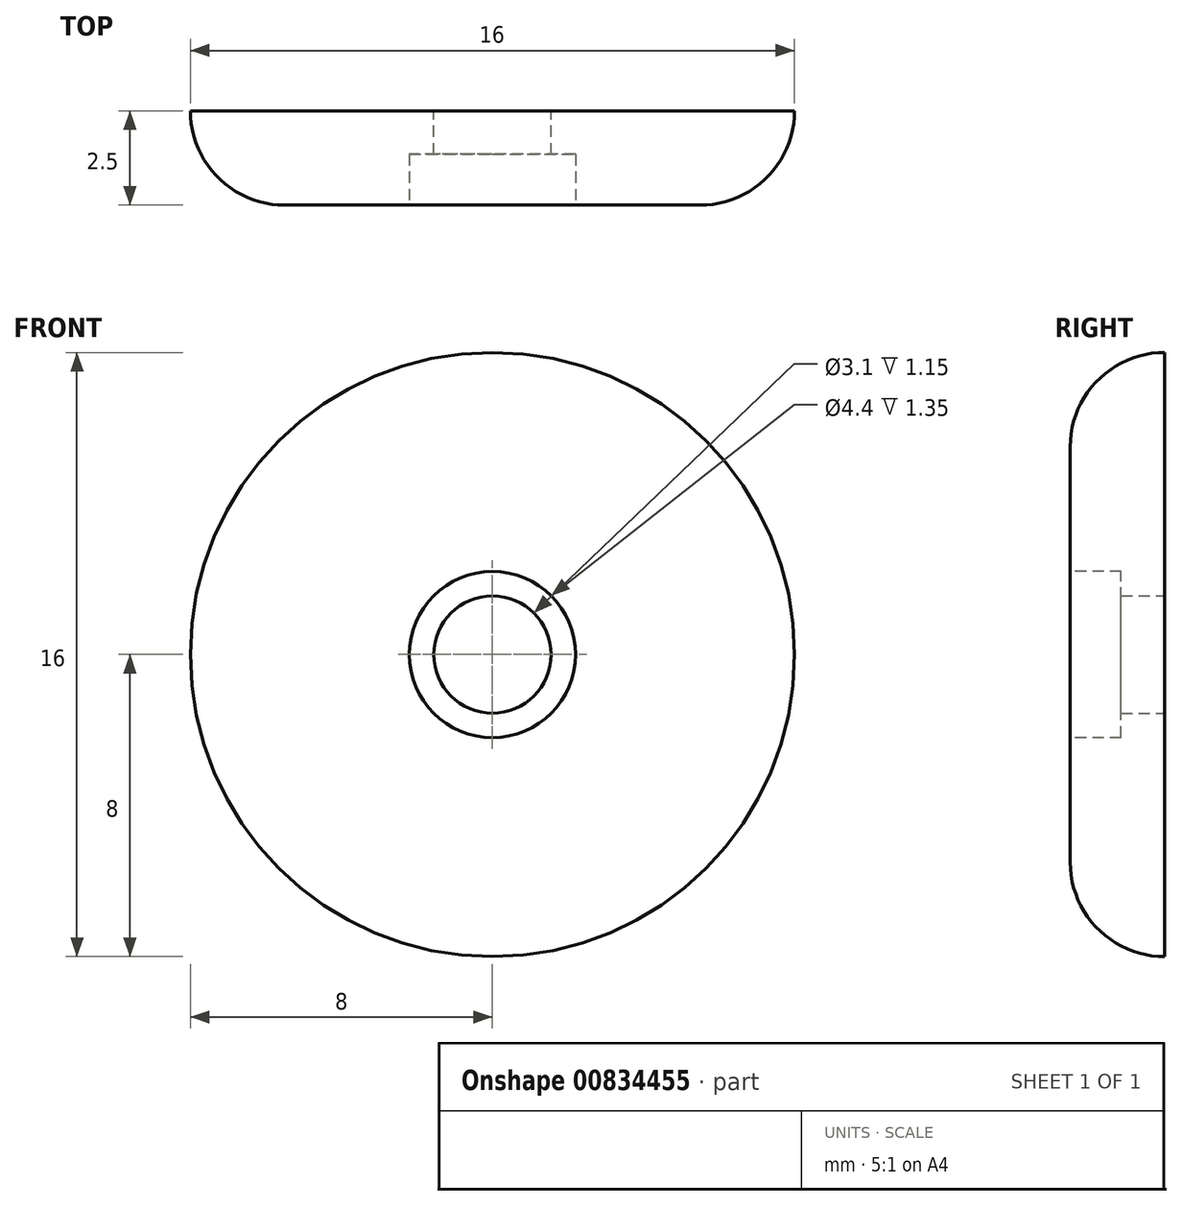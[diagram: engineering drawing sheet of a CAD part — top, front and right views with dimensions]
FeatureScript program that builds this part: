
annotation { "Feature Type Name" : "Feature", "Feature Type Description" : "" }
export const myFeature = defineFeature(function(context is Context, id is Id, definition is map)
    precondition{}
    {
        {
            var Q0;
            Q0=qCreatedBy(makeId("Front.planeOp"),FACE);
            var sketch = newSketch(context, id + "F0", { "sketchPlane" : qUnion([Q0])});
            skCircle(sketch, "E0", {"center": v(0, 0) * mm, "radius": 8 * mm});
            skSolve(sketch);
        }
        {
            var Q0;
            Q0 = qSketchRegion(id + "F0", true);
            extrude(context, id + "F1", {"entities" : qUnion([Q0]), "depth" : 2.5 * mm, "offsetDistance" : 25 * mm});
        }
        {
            var Q0;
            Q0=makeQuery(id+"F1.opExtrude","CAP_EDGE",EDGE,{"disambiguationData":[OSD([sQuery(id+"F0.wireOp",EDGE,"E0")])],"isStart":false});
            fillet(context, id + "F2", {"entities" : qUnion([Q0]), "radius" : 2.5 * mm, "tangentPropagation" : true, "allowEdgeOverflow" : false});
        }
        {
            var Q0;
            Q0=makeQuery(id+"F1.opExtrude","CAP_FACE",FACE,{"disambiguationData":[OSD([sQuery(id+"F0.wireOp",EDGE,"E0")])],"isStart":true});
            var sketch = newSketch(context, id + "F3", { "sketchPlane" : qUnion([Q0])});
            skCircle(sketch, "E1", {"center": v(0, 0) * mm, "radius": 1.55 * mm});
            skSolve(sketch);
        }
        {
            var Q0;
            Q0=makeQuery(id+"F3.imprint","IMPRINT",FACE,{"disambiguationData":[TD([[makeQuery(id+"F3.imprint","IMPRINT",EDGE,{"derivedFrom":sQuery(id+"F3.wireOp",EDGE,"E1")}),1.0]])]});
            extrude(context, id + "F4", {"entities" : qUnion([Q0]), "operationType" : NewBodyOperationType.REMOVE, "oppositeDirection" : true, "depth" : 25 * mm, "offsetDistance" : 25 * mm});
        }
        {
            var Q0;
            Q0=makeQuery(id+"F1.opExtrude","CAP_FACE",FACE,{"disambiguationData":[OSD([sQuery(id+"F0.wireOp",EDGE,"E0")])],"isStart":false});
            var sketch = newSketch(context, id + "F5", { "sketchPlane" : qUnion([Q0])});
            skCircle(sketch, "E2", {"center": v(0, 0) * mm, "radius": 2.2 * mm});
            skSolve(sketch);
        }
        {
            var Q0;
            Q0=makeQuery(id+"F5.imprint","IMPRINT",FACE,{"disambiguationData":[TD([[makeQuery(id+"F5.imprint","IMPRINT",EDGE,{"derivedFrom":sQuery(id+"F5.wireOp",EDGE,"E2")}),1.0]])]});
            extrude(context, id + "F6", {"entities" : qUnion([Q0]), "operationType" : NewBodyOperationType.REMOVE, "oppositeDirection" : true, "depth" : 1.35 * mm, "offsetDistance" : 25 * mm});
        }
    });
